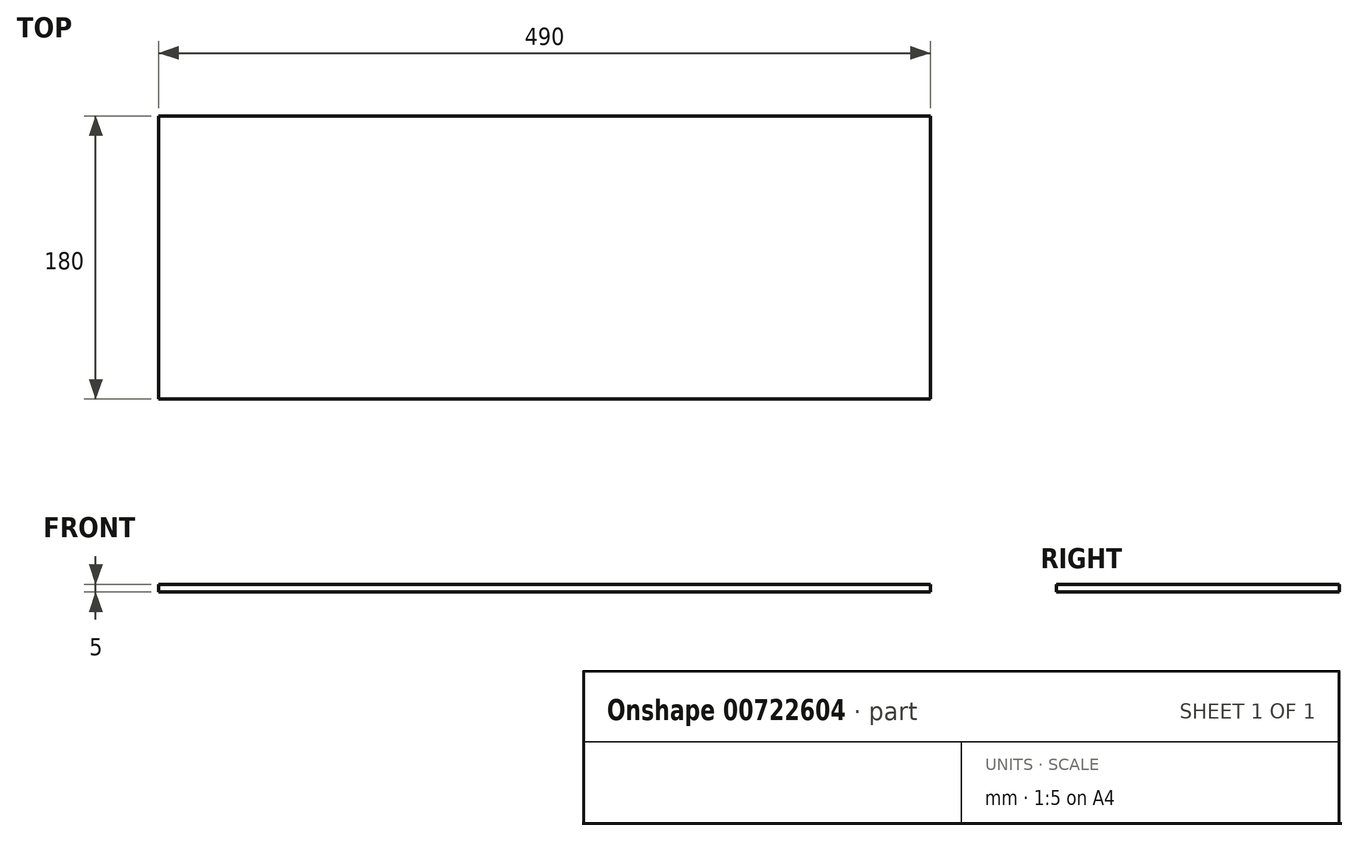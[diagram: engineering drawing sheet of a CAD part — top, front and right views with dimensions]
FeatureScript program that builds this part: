
annotation { "Feature Type Name" : "Feature", "Feature Type Description" : "" }
export const myFeature = defineFeature(function(context is Context, id is Id, definition is map)
    precondition{}
    {
        {
            var Q0;
            Q0=qCreatedBy(makeId("Front.planeOp"),FACE);
            var sketch = newSketch(context, id + "F0", { "sketchPlane" : qUnion([Q0])});
            skPoint(sketch, "E0.middle", {"position": v(0, 0) * mm});
            skLineSegment(sketch, "E1.bottom", {"start": v(-245, -2.5) * mm, "end": v(245, -2.5) * mm});
            skLineSegment(sketch, "E1.top", {"start": v(-245, 2.5) * mm, "end": v(245, 2.5) * mm});
            skLineSegment(sketch, "E1.left", {"start": v(-245, -2.5) * mm, "end": v(-245, 2.5) * mm});
            skLineSegment(sketch, "E1.right", {"start": v(245, -2.5) * mm, "end": v(245, 2.5) * mm});
            skSolve(sketch);
        }
        {
            var Q0;
            Q0=makeQuery(id+"F0.imprint","IMPRINT",FACE,{"disambiguationData":[TD([[makeQuery(id+"F0.imprint","IMPRINT",EDGE,{"derivedFrom":sQuery(id+"F0.wireOp",EDGE,"E1.bottom")}),1.0]])]});
            extrude(context, id + "F1", {"entities" : qUnion([Q0]), "endBound" : BoundingType.SYMMETRIC, "depth" : 180 * mm, "offsetDistance" : 25 * mm});
        }
    });
